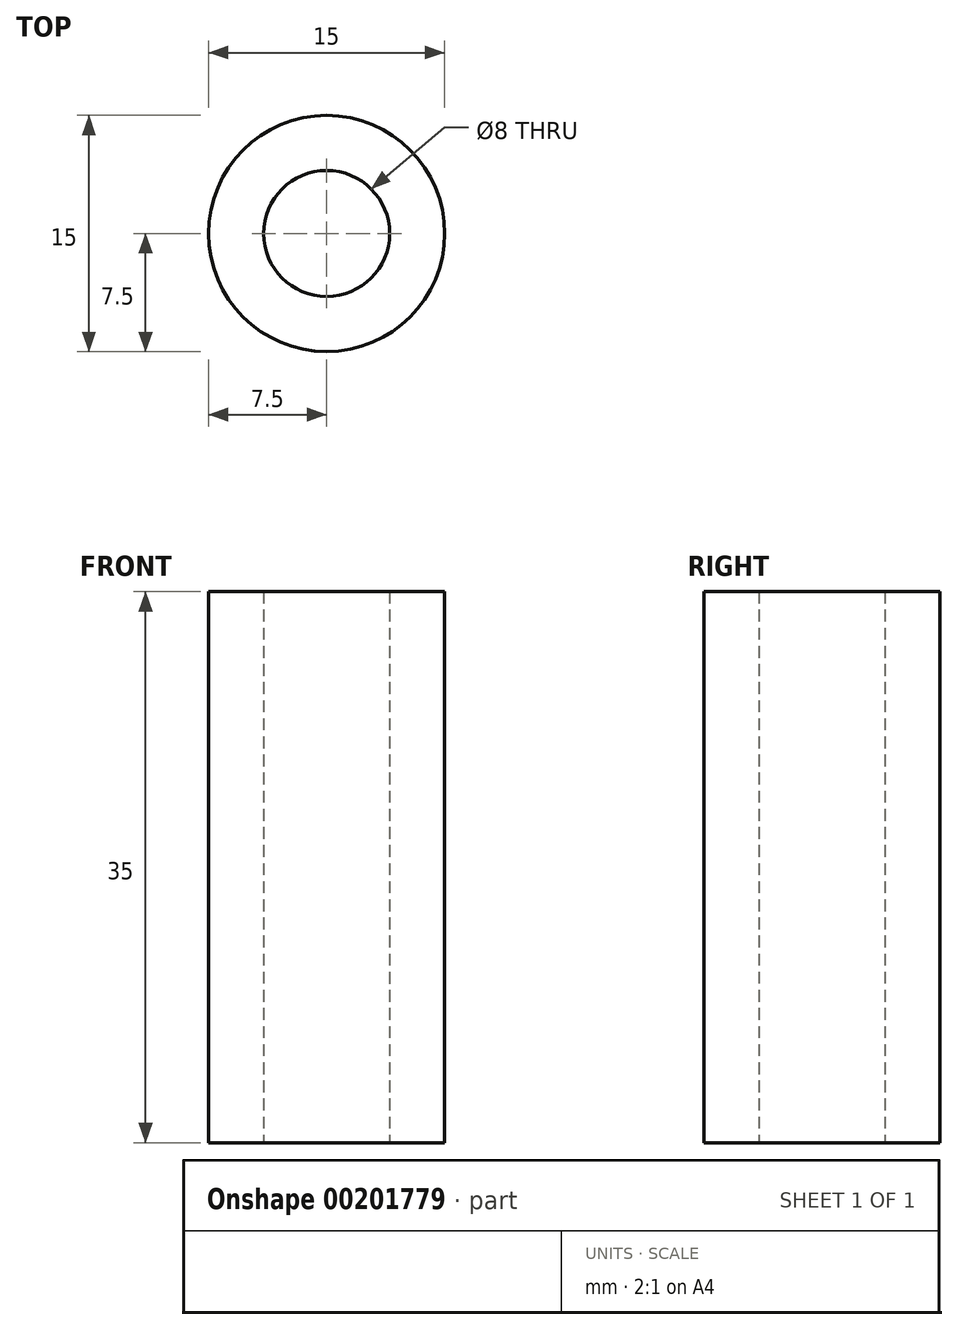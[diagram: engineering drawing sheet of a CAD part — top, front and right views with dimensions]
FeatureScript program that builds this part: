
annotation { "Feature Type Name" : "Feature", "Feature Type Description" : "" }
export const myFeature = defineFeature(function(context is Context, id is Id, definition is map)
    precondition{}
    {
        {
            var Q0;
            Q0=qCreatedBy(makeId("Top.planeOp"),FACE);
            var sketch = newSketch(context, id + "F0", { "sketchPlane" : qUnion([Q0])});
            skCircle(sketch, "E0", {"center": v(0, 0) * mm, "radius": 7.5 * mm});
            skCircle(sketch, "E1", {"center": v(0, 0) * mm, "radius": 4 * mm});
            skSolve(sketch);
        }
        {
            var Q0;
            Q0 = qSketchRegion(id + "F0", true);
            extrude(context, id + "F1", {"entities" : qUnion([Q0]), "depth" : 35 * mm});
        }
    });
